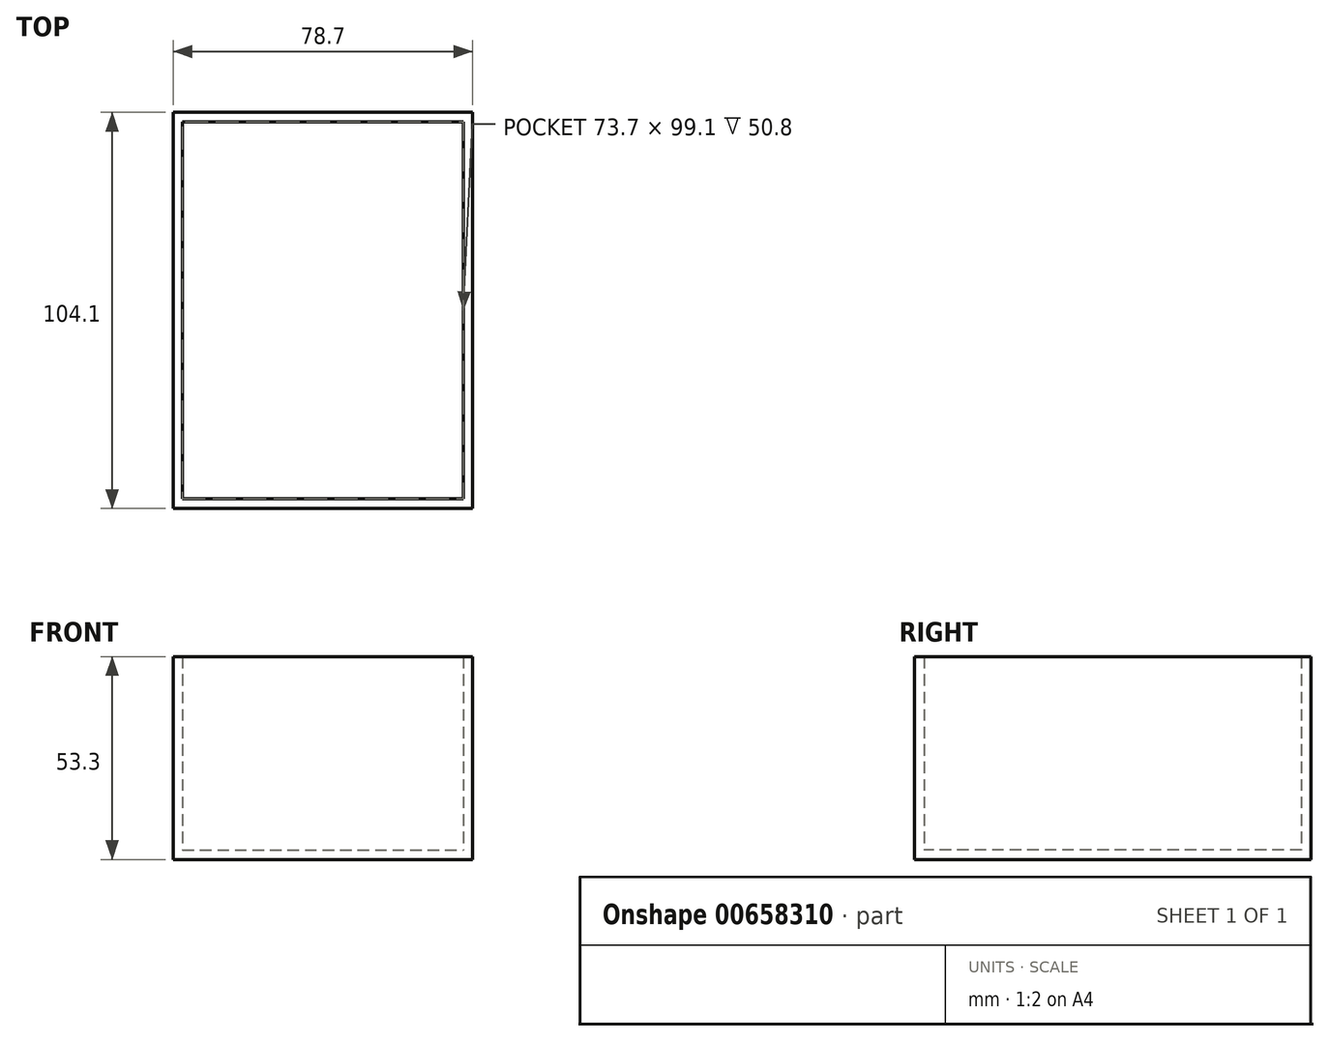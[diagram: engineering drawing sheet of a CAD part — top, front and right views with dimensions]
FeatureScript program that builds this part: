
annotation { "Feature Type Name" : "Feature", "Feature Type Description" : "" }
export const myFeature = defineFeature(function(context is Context, id is Id, definition is map)
    precondition{}
    {
        {
            var Q0;
            Q0=qCreatedBy(makeId("Top.planeOp"),FACE);
            var sketch = newSketch(context, id + "F0", { "sketchPlane" : qUnion([Q0])});
            skLineSegment(sketch, "E0.bottom", {"start": v(-52.16, 116.02) * mm, "end": v(21.54, 116.02) * mm});
            skLineSegment(sketch, "E0.top", {"start": v(-52.16, 16.92) * mm, "end": v(21.54, 16.92) * mm});
            skLineSegment(sketch, "E0.left", {"start": v(-52.16, 116.02) * mm, "end": v(-52.16, 16.92) * mm});
            skLineSegment(sketch, "E0.right", {"start": v(21.54, 116.02) * mm, "end": v(21.54, 16.92) * mm});
            skLineSegment(sketch, "E1.bottom", {"start": v(-54.66, 118.52) * mm, "end": v(24.04, 118.52) * mm});
            skLineSegment(sketch, "E1.top", {"start": v(-54.66, 14.42) * mm, "end": v(24.04, 14.42) * mm});
            skLineSegment(sketch, "E1.left", {"start": v(-54.66, 118.52) * mm, "end": v(-54.66, 14.42) * mm});
            skLineSegment(sketch, "E1.right", {"start": v(24.04, 118.52) * mm, "end": v(24.04, 14.42) * mm});
            skSolve(sketch);
        }
        {
            var Q0;
            Q0=makeQuery(id+"F0.imprint","IMPRINT",FACE,{"disambiguationData":[TD([[makeQuery(id+"F0.imprint","IMPRINT",EDGE,{"derivedFrom":sQuery(id+"F0.wireOp",EDGE,"E0.bottom")}),-1.0]])]});
            extrude(context, id + "F1", {"entities" : qUnion([Q0]), "depth" : 2.5 * mm, "offsetDistance" : 25 * mm});
        }
        {
            var Q0;
            Q0=makeQuery(id+"F0.imprint","IMPRINT",FACE,{"disambiguationData":[TD([[makeQuery(id+"F0.imprint","IMPRINT",EDGE,{"derivedFrom":sQuery(id+"F0.wireOp",EDGE,"E0.bottom")}),1.0]])]});
            extrude(context, id + "F2", {"entities" : qUnion([Q0]), "operationType" : NewBodyOperationType.ADD, "depth" : 53.3 * mm, "offsetDistance" : 25 * mm});
        }
    });
